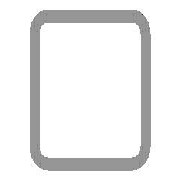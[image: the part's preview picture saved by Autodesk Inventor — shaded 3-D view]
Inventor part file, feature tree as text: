
AUTODESK INVENTOR PART (.ipt)
format: ipt  version: 2025.3 (Build 293356030, 356C)  size: 148,992 bytes
history: native  units: mm (DEFAULTED — no unit token found)
features: other x4, plane x3, split x2, sketch x1
ambient origin geometry x8: Origin, YZ Plane, XZ Plane, XY Plane, X Axis, Y Axis, Z Axis, Center Point
bodies: Solid1 (feature_tree), Body (feature_tree)
feature tree (10):
  parser-record x1  (decoder bookkeeping rows leaked as tree rows — omitted from the tree; the rows remain in map.json)
  other  "Driven Length"
  other  "Start Plane"
  other  "End Plane"
  plane  "Work Plane4"
  split  "Split1"
  plane  "Work Plane5"
  split  "Split2"
  sketch  "Sketch3"  dims[d3=826.981276mm d4=0.0mm d7=4.0mm d9=40.0mm d11=40.0mm d12=2.0mm d13=71.810467mm d14=898.791742mm d15=20.0mm d16=20.0mm d17=90.0deg d18=826.981276mm]
  plane  "Work Plane3"
